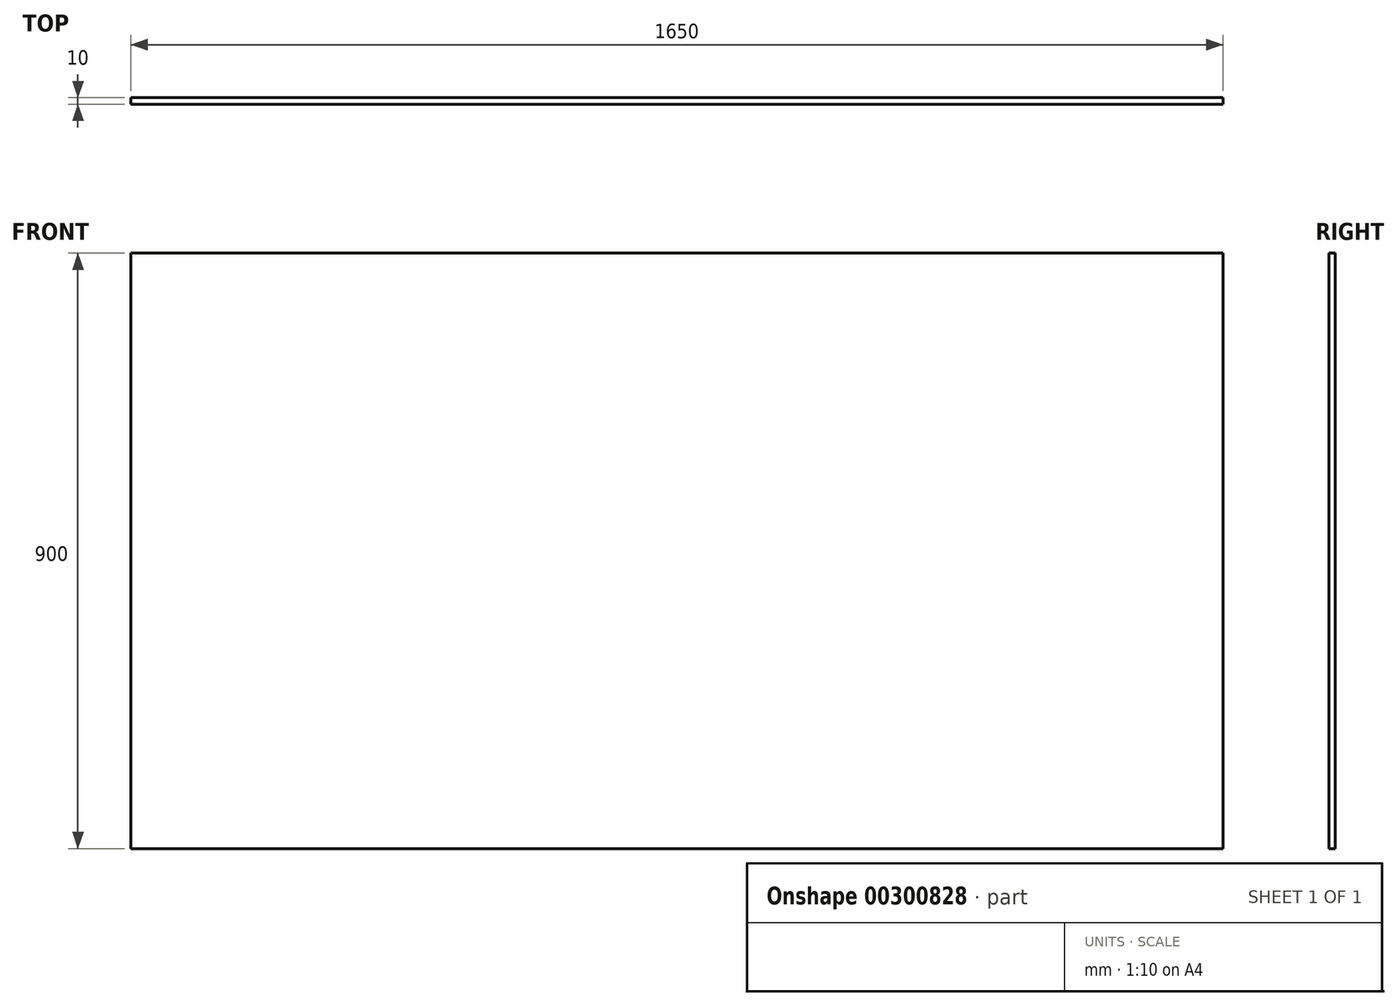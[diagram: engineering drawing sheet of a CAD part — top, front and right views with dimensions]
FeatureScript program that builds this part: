
annotation { "Feature Type Name" : "Feature", "Feature Type Description" : "" }
export const myFeature = defineFeature(function(context is Context, id is Id, definition is map)
    precondition{}
    {
        {
            var Q0;
            Q0=qCreatedBy(makeId("Front.planeOp"),FACE);
            var sketch = newSketch(context, id + "F0", { "sketchPlane" : qUnion([Q0])});
            skLineSegment(sketch, "E0.bottom", {"start": v(0, 0) * mm, "end": v(1650, 0) * mm});
            skLineSegment(sketch, "E0.top", {"start": v(0, -900) * mm, "end": v(1650, -900) * mm});
            skLineSegment(sketch, "E0.left", {"start": v(0, 0) * mm, "end": v(0, -900) * mm});
            skLineSegment(sketch, "E0.right", {"start": v(1650, 0) * mm, "end": v(1650, -900) * mm});
            skSolve(sketch);
        }
        {
            var Q0;
            Q0=makeQuery(id+"F0.imprint","IMPRINT",FACE,{"disambiguationData":[TD([[makeQuery(id+"F0.imprint","IMPRINT",EDGE,{"derivedFrom":sQuery(id+"F0.wireOp",EDGE,"E0.bottom")}),-1.0]])]});
            extrude(context, id + "F1", {"entities" : qUnion([Q0]), "depth" : 10 * mm});
        }
    });
